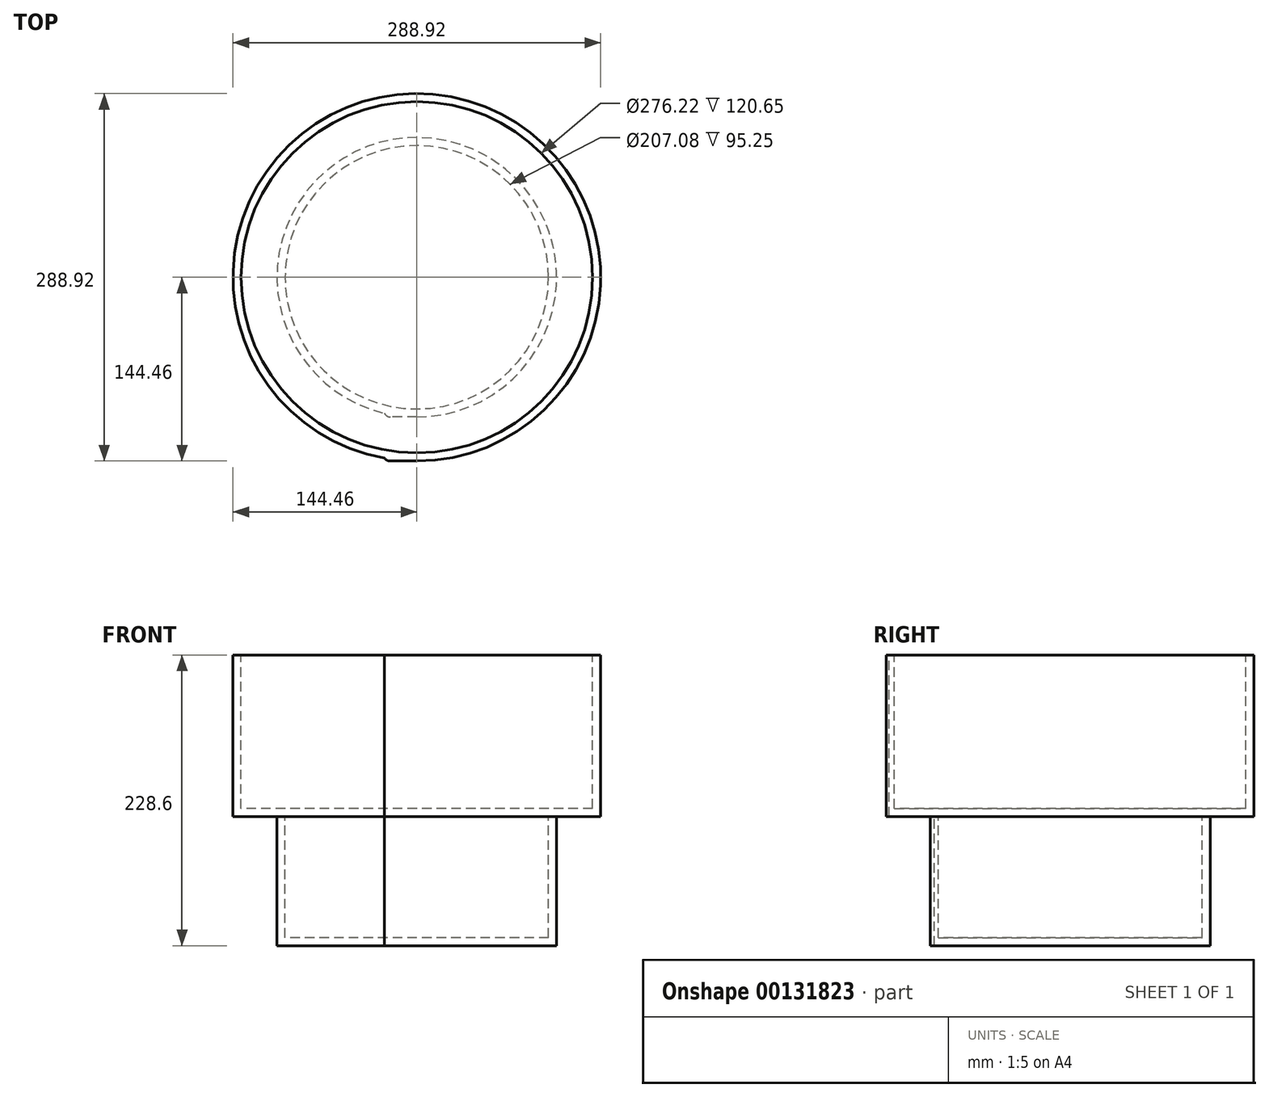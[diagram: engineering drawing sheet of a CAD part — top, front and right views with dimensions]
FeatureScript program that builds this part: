
annotation { "Feature Type Name" : "Feature", "Feature Type Description" : "" }
export const myFeature = defineFeature(function(context is Context, id is Id, definition is map)
    precondition{}
    {
        {
            var Q0;
            Q0=qCreatedBy(makeId("Right.planeOp"),FACE);
            var sketch = newSketch(context, id + "F0", { "sketchPlane" : qUnion([Q0])});
            skLineSegment(sketch, "E0", {"start": v(0, 0) * mm, "end": v(-144.46, 0) * mm});
            skLineSegment(sketch, "E1", {"start": v(-144.46, 0) * mm, "end": v(-144.46, 127) * mm});
            skLineSegment(sketch, "E2", {"start": v(-144.46, 127) * mm, "end": v(-138.11, 127) * mm});
            skLineSegment(sketch, "E3", {"start": v(-138.11, 127) * mm, "end": v(-138.11, 6.35) * mm});
            skLineSegment(sketch, "E4", {"start": v(-138.11, 6.35) * mm, "end": v(0, 6.35) * mm});
            skLineSegment(sketch, "E5", {"start": v(0, 6.35) * mm, "end": v(0, 0) * mm});
            skLineSegment(sketch, "E6", {"start": v(-109.9, 0) * mm, "end": v(-109.9, -101.6) * mm});
            skLineSegment(sketch, "E7", {"start": v(-109.9, -101.6) * mm, "end": v(0, -101.6) * mm});
            skLineSegment(sketch, "E8", {"start": v(0, -101.6) * mm, "end": v(0, -95.25) * mm});
            skLineSegment(sketch, "E9", {"start": v(0, -95.25) * mm, "end": v(-103.54, -95.25) * mm});
            skLineSegment(sketch, "E10", {"start": v(-103.54, -95.25) * mm, "end": v(-103.54, 0) * mm});
            skLineSegment(sketch, "E11", {"start": v(-103.54, 0) * mm, "end": v(-109.9, 0) * mm});
            skSolve(sketch);
        }
        {
            var Q0;
            Q0 = qSketchRegion(id + "F0", true);
            extrude(context, id + "F1", {"entities" : qUnion([Q0]), "depth" : 25.4 * mm});
        }
        {
            var Q0;
            Q0=makeQuery(id+"F1.opExtrude","CAP_FACE",FACE,{"disambiguationData":[OSD([sQuery(id+"F0.wireOp",EDGE,"E0"),sQuery(id+"F0.wireOp",EDGE,"E1"),sQuery(id+"F0.wireOp",EDGE,"E2"),sQuery(id+"F0.wireOp",EDGE,"E3"),sQuery(id+"F0.wireOp",EDGE,"E4"),sQuery(id+"F0.wireOp",EDGE,"E5"),sQuery(id+"F0.wireOp",EDGE,"E6"),sQuery(id+"F0.wireOp",EDGE,"E7"),sQuery(id+"F0.wireOp",EDGE,"E8"),sQuery(id+"F0.wireOp",EDGE,"E9"),sQuery(id+"F0.wireOp",EDGE,"E10")])],"isStart":false});
            var Q1;
            Q1=makeQuery(id+"F1.opExtrude","CAP_EDGE",EDGE,{"disambiguationData":[OSD([sQuery(id+"F0.wireOp",EDGE,"E5")])],"isStart":false});
            revolve(context, id + "F2", {"operationType" : NewBodyOperationType.ADD, "entities" : qUnion([Q0]), "axis" : qUnion([Q1]), "revolveType" : RevolveType.FULL});
        }
        {
            var Q0;
            Q0=makeQuery(id+"F1.opExtrude","CAP_EDGE",EDGE,{"disambiguationData":[OSD([sQuery(id+"F0.wireOp",EDGE,"E6")])],"isStart":true});
            var Q1;
            Q1=makeQuery(id+"F1.opExtrude","CAP_EDGE",EDGE,{"disambiguationData":[OSD([sQuery(id+"F0.wireOp",EDGE,"E6")])],"isStart":false});
            var Q2;
            Q2=makeQuery(id+"F1.opExtrude","CAP_EDGE",EDGE,{"disambiguationData":[OSD([sQuery(id+"F0.wireOp",EDGE,"E1")])],"isStart":true});
            var Q3;
            Q3=makeQuery(id+"F1.opExtrude","CAP_EDGE",EDGE,{"disambiguationData":[OSD([sQuery(id+"F0.wireOp",EDGE,"E1")])],"isStart":false});
            fillet(context, id + "F3", {"entities" : qUnion([Q0, Q1, Q2, Q3]), "radius" : 5.08 * mm, "tangentPropagation" : true, "allowEdgeOverflow" : false});
        }
    });
